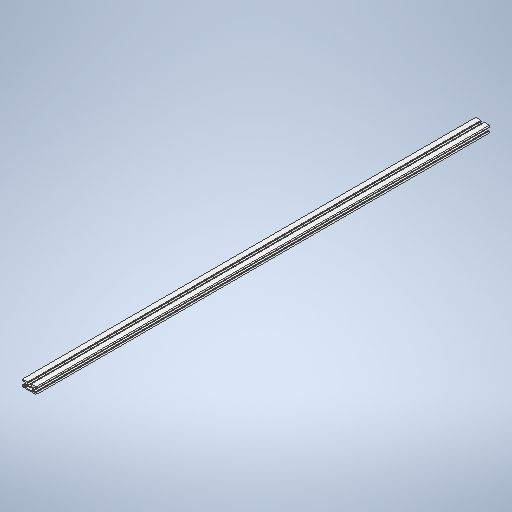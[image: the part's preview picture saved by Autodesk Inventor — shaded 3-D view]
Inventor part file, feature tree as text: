
AUTODESK INVENTOR PART (.ipt)
format: ipt  version: 2025.2 (Build 292293000, 293)  size: 364,032 bytes
history: native  units: mm
features: other x1, extrude x1, mirror x1, sketch x1
ambient origin geometry x8: Origin, YZ Plane, XZ Plane, XY Plane, X Axis, Y Axis, Z Axis, Center Point
bodies: Body1 (feature_tree)
feature tree (4):
  other  "Sólido1"
  extrude  "Extrusão1"  Depth=6.0mm
  mirror  "Espelhar1"
  sketch  "Esboço3"  dims[d33=15.0mm d34=6.0mm d35=30.0mm d36=2.0mm d37=6.2mm d38=2.0mm d39=3.0mm d40=6.2mm d41=2.0mm d43=3.0mm d44=2.0mm d45=2.0mm d46=2.0mm d47=0.5mm d52=0.5mm d61=1000.0mm d62=0.0mm d27=0.5mm d28=0.872665mm d29=0.5mm d30=0.872665mm]
